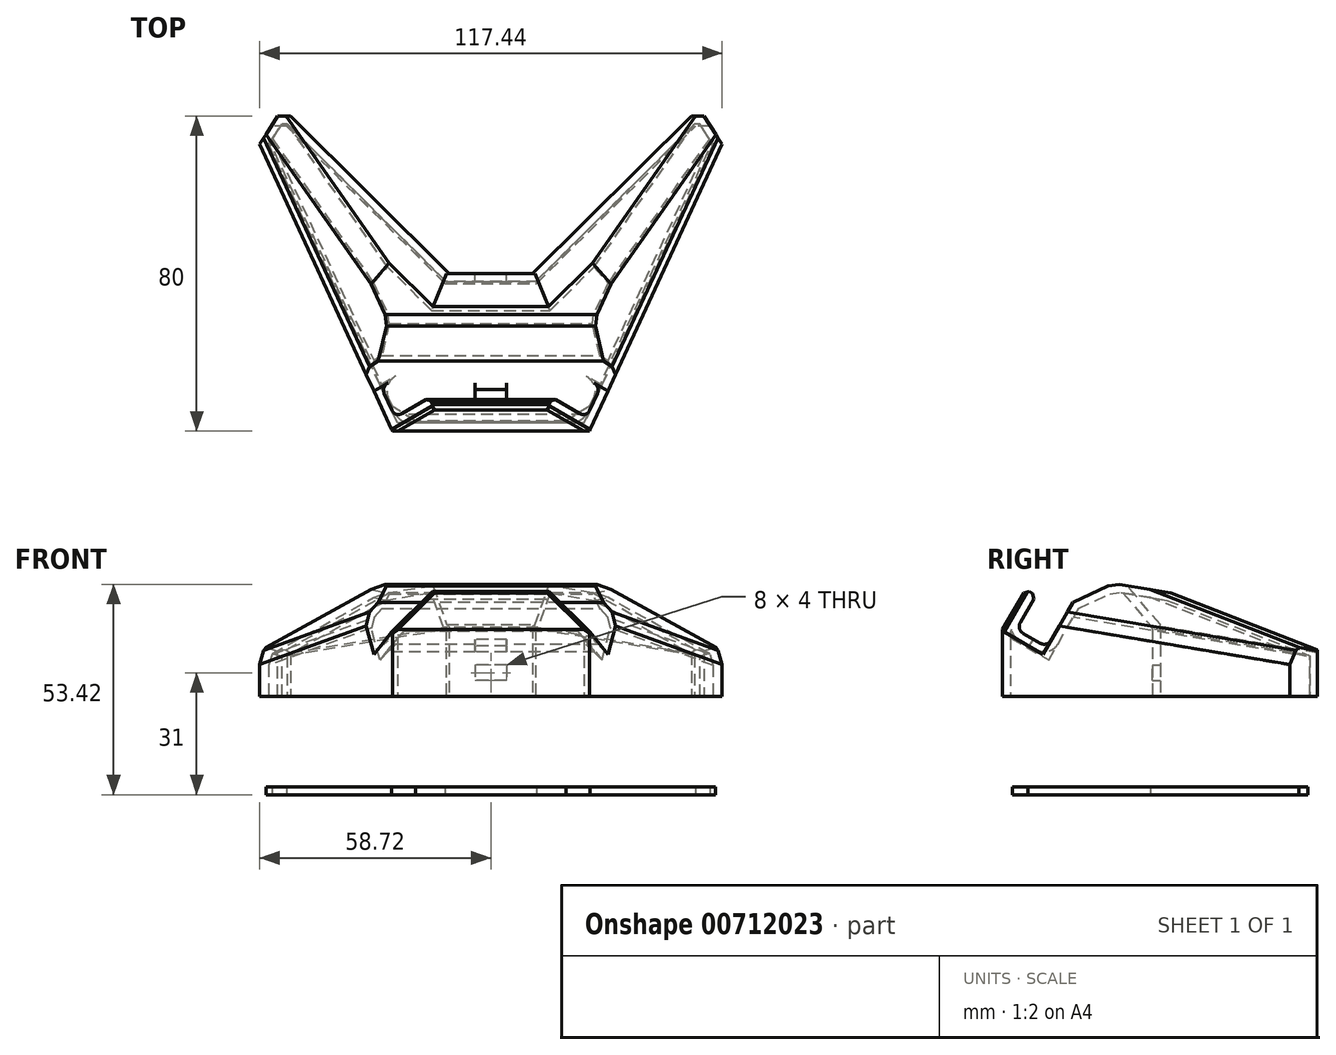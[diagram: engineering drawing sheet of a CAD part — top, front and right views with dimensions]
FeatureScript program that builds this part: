
annotation { "Feature Type Name" : "Feature", "Feature Type Description" : "" }
export const myFeature = defineFeature(function(context is Context, id is Id, definition is map)
    precondition{}
    {
        {
            var Q0;
            Q0=qCreatedBy(makeId("Right.planeOp"),FACE);
            var sketch = newSketch(context, id + "F0", { "sketchPlane" : qUnion([Q0])});
            skLineSegment(sketch, "E0", {"start": v(-41.49, 14.24) * mm, "end": v(-32.49, 29.83) * mm});
            skLineSegment(sketch, "E1", {"start": v(26.26, 20) * mm, "end": v(26.26, 0) * mm});
            skLineSegment(sketch, "E2", {"start": v(26.26, 0) * mm, "end": v(-53.74, 0) * mm});
            skLineSegment(sketch, "E3", {"start": v(-53.74, 0) * mm, "end": v(-53.74, 17) * mm});
            skLineSegment(sketch, "E4", {"start": v(-53.74, 17) * mm, "end": v(-47.88, 27.17) * mm});
            skLineSegment(sketch, "E5", {"start": v(-47.88, 27.17) * mm, "end": v(-45.28, 25.67) * mm});
            skLineSegment(sketch, "E6", {"start": v(-45.28, 25.67) * mm, "end": v(-49.28, 18.74) * mm});
            skLineSegment(sketch, "E7", {"start": v(-48.55, 16) * mm, "end": v(-44.22, 13.5) * mm});
            skPoint(sketch, "E8.visualSharp", {"position": v(-50.28, 17) * mm});
            skArc(sketch, "E8.filletArc", {"start": v(-49.28, 18.74) * mm, "mid": v(-49.48, 17.22) * mm, "end": v(-48.55, 16) * mm});
            skPoint(sketch, "E9.visualSharp", {"position": v(-42.49, 12.5) * mm});
            skArc(sketch, "E9.filletArc", {"start": v(-44.22, 13.5) * mm, "mid": v(-42.7, 13.3) * mm, "end": v(-41.49, 14.24) * mm});
            skLineSegment(sketch, "E10", {"start": v(-32.49, 29.83) * mm, "end": v(26.26, 20) * mm});
            skSolve(sketch);
        }
        {
            var Q0;
            Q0=makeQuery(id+"F0.imprint","IMPRINT",FACE,{"disambiguationData":[TD([[makeQuery(id+"F0.imprint","IMPRINT",EDGE,{"derivedFrom":sQuery(id+"F0.wireOp",EDGE,"E0")}),-1.0]])]});
            extrude(context, id + "F1", {"entities" : qUnion([Q0]), "endBound" : BoundingType.SYMMETRIC, "depth" : (114 + 10) * mm, "offsetDistance" : 25 * mm});
        }
        {
            var Q0;
            Q0=makeQuery(id+"F1.opExtrude","SWEPT_FACE",FACE,{"disambiguationData":[OSD([sQuery(id+"F0.wireOp",EDGE,"E2")])]});
            var sketch = newSketch(context, id + "F2", { "sketchPlane" : qUnion([Q0])});
            skLineSegment(sketch, "E11", {"start": v(62, 13.74) * mm, "end": v(-36.83, 13.74) * mm, "construction": true});
            skLineSegment(sketch, "E12", {"start": v(-62, -26.26) * mm, "end": v(-25, 53.74) * mm});
            skLineSegment(sketch, "E13", {"start": v(-10.58, 13.74) * mm, "end": v(-50.92, -26.26) * mm});
            skLineSegment(sketch, "E14.MirrorCS", {"start": v(10.58, 13.74) * mm, "end": v(50.92, -26.26) * mm});
            skLineSegment(sketch, "E15.MirrorCS", {"start": v(62, -26.26) * mm, "end": v(25, 53.74) * mm});
            skLineSegment(sketch, "E16", {"start": v(-10.58, 13.74) * mm, "end": v(10.58, 13.74) * mm});
            skSolve(sketch);
        }
        {
            var Q0;
            {var subQ0=sQuery(id+"F2.wireOp",EDGE,"E12");Q0=makeQuery(id+"F2.imprint","IMPRINT",FACE,{"disambiguationData":[TD([[makeQuery(id+"F2.imprint","IMPRINT",EDGE,{"derivedFrom":subQ0}),1.0]])]});}
            var Q1;
            {var subQ0=sQuery(id+"F2.wireOp",EDGE,"E13");Q1=makeQuery(id+"F2.imprint","IMPRINT",FACE,{"disambiguationData":[TD([[makeQuery(id+"F2.imprint","IMPRINT",EDGE,{"derivedFrom":subQ0}),1.0]])]});}
            var Q2;
            {var subQ0=sQuery(id+"F2.wireOp",EDGE,"E15.MirrorCS");Q2=makeQuery(id+"F2.imprint","IMPRINT",FACE,{"disambiguationData":[TD([[makeQuery(id+"F2.imprint","IMPRINT",EDGE,{"derivedFrom":subQ0}),-1.0]])]});}
            extrude(context, id + "F3", {"entities" : qUnion([Q0, Q1, Q2]), "operationType" : NewBodyOperationType.REMOVE, "endBound" : BoundingType.THROUGH_ALL, "oppositeDirection" : true, "depth" : 25 * mm, "offsetDistance" : 25 * mm});
        }
        {
            var Q0;
            Q0=makeQuery(id+"F3.boolean.opBoolean","INTERSECT",EDGE,{"derivedFrom":[makeQuery(id+"F1.opExtrude","SWEPT_FACE",FACE,{"disambiguationData":[OSD([sQuery(id+"F0.wireOp",EDGE,"E10")])]}),makeQuery(id+"F3.opExtrude","SWEPT_FACE",FACE,{"disambiguationData":[OSD([sQuery(id+"F2.wireOp",EDGE,"E12")])]})]});
            var Q1;
            Q1=makeQuery(id+"F3.boolean.opBoolean","INTERSECT",EDGE,{"derivedFrom":[makeQuery(id+"F1.opExtrude","SWEPT_FACE",FACE,{"disambiguationData":[OSD([sQuery(id+"F0.wireOp",EDGE,"E10")])]}),makeQuery(id+"F3.opExtrude","SWEPT_FACE",FACE,{"disambiguationData":[OSD([sQuery(id+"F2.wireOp",EDGE,"E13")])]})]});
            var Q2;
            Q2=makeQuery(id+"F3.boolean.opBoolean","INTERSECT",EDGE,{"derivedFrom":[makeQuery(id+"F1.opExtrude","SWEPT_FACE",FACE,{"disambiguationData":[OSD([sQuery(id+"F0.wireOp",EDGE,"E10")])]}),makeQuery(id+"F3.opExtrude","SWEPT_FACE",FACE,{"disambiguationData":[OSD([sQuery(id+"F2.wireOp",EDGE,"E16")])]})]});
            var Q3;
            Q3=makeQuery(id+"F3.boolean.opBoolean","INTERSECT",EDGE,{"derivedFrom":[makeQuery(id+"F1.opExtrude","SWEPT_FACE",FACE,{"disambiguationData":[OSD([sQuery(id+"F0.wireOp",EDGE,"E10")])]}),makeQuery(id+"F3.opExtrude","SWEPT_FACE",FACE,{"disambiguationData":[OSD([sQuery(id+"F2.wireOp",EDGE,"E14.MirrorCS")])]})]});
            var Q4;
            Q4=makeQuery(id+"F3.boolean.opBoolean","INTERSECT",EDGE,{"derivedFrom":[makeQuery(id+"F1.opExtrude","SWEPT_FACE",FACE,{"disambiguationData":[OSD([sQuery(id+"F0.wireOp",EDGE,"E10")])]}),makeQuery(id+"F3.opExtrude","SWEPT_FACE",FACE,{"disambiguationData":[OSD([sQuery(id+"F2.wireOp",EDGE,"E15.MirrorCS")])]})]});
            var Q5;
            Q5=makeQuery(id+"F1.opExtrude","SWEPT_EDGE",EDGE,{"disambiguationData":[OSD([sQuery(id+"F0.wireOp",EDGE,"E0"),sQuery(id+"F0.wireOp",EDGE,"E10")])]});
            chamfer(context, id + "F4", {"entities" : qUnion([Q0, Q1, Q2, Q3, Q4, Q5]), "width" : 10 * mm, "tangentPropagation" : true});
        }
        {
            var Q0;
            {var subQ0=makeQuery(id+"F1.opExtrude","SWEPT_FACE",FACE,{"disambiguationData":[OSD([sQuery(id+"F0.wireOp",EDGE,"E10")])]});Q0=makeQuery(id+"F4.opChamfer","BLEND_EDGE",EDGE,{"blendedFrom":[makeQuery(id+"F3.boolean.opBoolean","INTERSECT",EDGE,{"derivedFrom":[subQ0,makeQuery(id+"F3.opExtrude","SWEPT_FACE",FACE,{"disambiguationData":[OSD([sQuery(id+"F2.wireOp",EDGE,"E15.MirrorCS")])]})]}),makeQuery(id+"F3.boolean.opBoolean","INTERSECT",EDGE,{"derivedFrom":[subQ0,makeQuery(id+"F3.opExtrude","SWEPT_FACE",FACE,{"disambiguationData":[OSD([sQuery(id+"F2.wireOp",EDGE,"E14.MirrorCS")])]})]})],"blendedInto":[]});}
            var Q1;
            {var subQ0=makeQuery(id+"F1.opExtrude","SWEPT_FACE",FACE,{"disambiguationData":[OSD([sQuery(id+"F0.wireOp",EDGE,"E10")])]});Q1=makeQuery(id+"F4.opChamfer","BLEND_EDGE",EDGE,{"blendedFrom":[makeQuery(id+"F3.boolean.opBoolean","INTERSECT",EDGE,{"derivedFrom":[subQ0,makeQuery(id+"F3.opExtrude","SWEPT_FACE",FACE,{"disambiguationData":[OSD([sQuery(id+"F2.wireOp",EDGE,"E12")])]})]}),makeQuery(id+"F3.boolean.opBoolean","INTERSECT",EDGE,{"derivedFrom":[subQ0,makeQuery(id+"F3.opExtrude","SWEPT_FACE",FACE,{"disambiguationData":[OSD([sQuery(id+"F2.wireOp",EDGE,"E13")])]})]})],"blendedInto":[]});}
            var Q2;
            {var subQ0=makeQuery(id+"F3.opExtrude","SWEPT_FACE",FACE,{"disambiguationData":[OSD([sQuery(id+"F2.wireOp",EDGE,"E15.MirrorCS")])]});Q2=makeQuery(id+"F4.opChamfer","BLEND_EDGE",EDGE,{"blendedFrom":[makeQuery(id+"F3.boolean.opBoolean","INTERSECT",EDGE,{"derivedFrom":[makeQuery(id+"F1.opExtrude","SWEPT_FACE",FACE,{"disambiguationData":[OSD([sQuery(id+"F0.wireOp",EDGE,"E10")])]}),subQ0]}),makeQuery(id+"F3.boolean.opBoolean","COPY",FACE,{"derivedFrom":subQ0})],"blendedInto":[makeQuery(id+"F3.boolean.opBoolean","COPY",FACE,{"derivedFrom":subQ0})]});}
            var Q3;
            {var subQ0=makeQuery(id+"F3.opExtrude","SWEPT_FACE",FACE,{"disambiguationData":[OSD([sQuery(id+"F2.wireOp",EDGE,"E12")])]});Q3=makeQuery(id+"F4.opChamfer","BLEND_EDGE",EDGE,{"blendedFrom":[makeQuery(id+"F3.boolean.opBoolean","INTERSECT",EDGE,{"derivedFrom":[makeQuery(id+"F1.opExtrude","SWEPT_FACE",FACE,{"disambiguationData":[OSD([sQuery(id+"F0.wireOp",EDGE,"E10")])]}),subQ0]}),makeQuery(id+"F3.boolean.opBoolean","COPY",FACE,{"derivedFrom":subQ0})],"blendedInto":[makeQuery(id+"F3.boolean.opBoolean","COPY",FACE,{"derivedFrom":subQ0})]});}
            var Q4;
            {var subQ0=sQuery(id+"F0.wireOp",EDGE,"E10");Q4=makeQuery(id+"F4.opChamfer","BLEND_EDGE",EDGE,{"blendedFrom":[makeQuery(id+"F1.opExtrude","SWEPT_EDGE",EDGE,{"disambiguationData":[OSD([sQuery(id+"F0.wireOp",EDGE,"E0"),subQ0])]}),makeQuery(id+"F1.opExtrude","SWEPT_FACE",FACE,{"disambiguationData":[OSD([subQ0])]})],"blendedInto":[makeQuery(id+"F1.opExtrude","SWEPT_FACE",FACE,{"disambiguationData":[OSD([subQ0])]})]});}
            chamfer(context, id + "F5", {"entities" : qUnion([Q0, Q1, Q2, Q3, Q4]), "width" : 5 * mm, "tangentPropagation" : true});
        }
        {
            var Q0;
            Q0=makeQuery(id+"F3.boolean.opBoolean","INTERSECT",EDGE,{"derivedFrom":[makeQuery(id+"F1.opExtrude","SWEPT_FACE",FACE,{"disambiguationData":[OSD([sQuery(id+"F0.wireOp",EDGE,"E5")])]}),makeQuery(id+"F3.opExtrude","SWEPT_FACE",FACE,{"disambiguationData":[OSD([sQuery(id+"F2.wireOp",EDGE,"E15.MirrorCS")])]})]});
            var Q1;
            Q1=makeQuery(id+"F3.boolean.opBoolean","INTERSECT",EDGE,{"derivedFrom":[makeQuery(id+"F1.opExtrude","SWEPT_FACE",FACE,{"disambiguationData":[OSD([sQuery(id+"F0.wireOp",EDGE,"E5")])]}),makeQuery(id+"F3.opExtrude","SWEPT_FACE",FACE,{"disambiguationData":[OSD([sQuery(id+"F2.wireOp",EDGE,"E12")])]})]});
            var Q2;
            Q2=makeQuery(id+"F3.boolean.opBoolean","COPY",EDGE,{"derivedFrom":makeQuery(id+"F3.opExtrude","SWEPT_EDGE",EDGE,{"disambiguationData":[OSD([sQuery(id+"F0.wireOp",EDGE,"E2"),sQuery(id+"F0.wireOp",EDGE,"E3"),sQuery(id+"F2.wireOp",EDGE,"E15.MirrorCS")])]})});
            var Q3;
            Q3=makeQuery(id+"F3.boolean.opBoolean","COPY",EDGE,{"derivedFrom":makeQuery(id+"F3.opExtrude","SWEPT_EDGE",EDGE,{"disambiguationData":[OSD([sQuery(id+"F0.wireOp",EDGE,"E2"),sQuery(id+"F0.wireOp",EDGE,"E3"),sQuery(id+"F2.wireOp",EDGE,"E12")])]})});
            chamfer(context, id + "F6", {"entities" : qUnion([Q0, Q1, Q2, Q3]), "width" : 10 * mm, "tangentPropagation" : true});
        }
        {
            var Q0;
            {var subQ0=sQuery(id+"F0.wireOp",EDGE,"E1");Q0=makeQuery(id+"F3.boolean.opBoolean","MERGE",EDGE,{"derivedFrom":[makeQuery(id+"F1.opExtrude","CAP_EDGE",EDGE,{"disambiguationData":[OSD([subQ0])],"isStart":false}),makeQuery(id+"F3.opExtrude","SWEPT_EDGE",EDGE,{"disambiguationData":[OSD([subQ0,sQuery(id+"F0.wireOp",EDGE,"E2"),sQuery(id+"F2.wireOp",EDGE,"E15.MirrorCS")])]})]});}
            var Q1;
            {var subQ0=sQuery(id+"F0.wireOp",EDGE,"E1");Q1=makeQuery(id+"F3.boolean.opBoolean","MERGE",EDGE,{"derivedFrom":[makeQuery(id+"F1.opExtrude","CAP_EDGE",EDGE,{"disambiguationData":[OSD([subQ0])],"isStart":true}),makeQuery(id+"F3.opExtrude","SWEPT_EDGE",EDGE,{"disambiguationData":[OSD([subQ0,sQuery(id+"F0.wireOp",EDGE,"E2"),sQuery(id+"F2.wireOp",EDGE,"E12")])]})]});}
            chamfer(context, id + "F7", {"entities" : qUnion([Q0, Q1]), "width" : 5 * mm, "tangentPropagation" : true});
        }
        {
            var Q0;
            Q0=makeQuery(id+"F1.opExtrude","SWEPT_FACE",FACE,{"disambiguationData":[OSD([sQuery(id+"F0.wireOp",EDGE,"E2")])]});
            shell(context, id + "F8", {"entities" : qUnion([Q0]), "thickness" : 2 * mm});
        }
        {
            var Q0;
            Q0=makeQuery(id+"F3.boolean.opBoolean","COPY",FACE,{"derivedFrom":makeQuery(id+"F3.opExtrude","SWEPT_FACE",FACE,{"disambiguationData":[OSD([sQuery(id+"F2.wireOp",EDGE,"E16")])]})});
            var sketch = newSketch(context, id + "F9", { "sketchPlane" : qUnion([Q0])});
            skLineSegment(sketch, "E17.bottom", {"start": v(-4, 8) * mm, "end": v(4, 8) * mm});
            skLineSegment(sketch, "E17.top", {"start": v(-4, 4) * mm, "end": v(4, 4) * mm});
            skLineSegment(sketch, "E17.left", {"start": v(-4, 8) * mm, "end": v(-4, 4) * mm});
            skLineSegment(sketch, "E17.right", {"start": v(4, 8) * mm, "end": v(4, 4) * mm});
            skLineSegment(sketch, "E18", {"start": v(0, 4) * mm, "end": v(0, 0) * mm, "construction": true});
            skSolve(sketch);
        }
        {
            var Q0;
            Q0 = qSketchRegion(id + "F9", true);
            var Q1;
            Q1=makeQuery(id+"F8.opShell","OFFSET_FACE",FACE,{"disambiguationData":[OSD([sQuery(id+"F2.wireOp",EDGE,"E16")])]});
            extrude(context, id + "F10", {"entities" : qUnion([Q0]), "operationType" : NewBodyOperationType.REMOVE, "endBound" : BoundingType.UP_TO_SURFACE, "oppositeDirection" : true, "depth" : 25 * mm, "endBoundEntityFace" : qUnion([Q1]), "offsetDistance" : 25 * mm});
        }
        {
            var Q0;
            Q0=makeQuery(id+"F1.opExtrude","SWEPT_FACE",FACE,{"disambiguationData":[OSD([sQuery(id+"F0.wireOp",EDGE,"E7")])]});
            var sketch = newSketch(context, id + "F11", { "sketchPlane" : qUnion([Q0])});
            skLineSegment(sketch, "E19.bottom", {"start": v(4, -47.05) * mm, "end": v(-4, -47.05) * mm});
            skLineSegment(sketch, "E19.top", {"start": v(4, -43.05) * mm, "end": v(-4, -43.05) * mm});
            skLineSegment(sketch, "E19.left", {"start": v(4, -47.05) * mm, "end": v(4, -43.05) * mm});
            skLineSegment(sketch, "E19.right", {"start": v(-4, -47.05) * mm, "end": v(-4, -43.05) * mm});
            skPoint(sketch, "E20.endSnap0", {"position": v(0, -50.05) * mm});
            skLineSegment(sketch, "E21.0", {"start": v(30.67, -43.05) * mm, "end": v(-30.67, -43.05) * mm});
            skLineSegment(sketch, "E22", {"start": v(0, -43.05) * mm, "end": v(0, -43.05) * mm});
            skSolve(sketch);
        }
        {
            var Q0;
            Q0 = qSketchRegion(id + "F11", true);
            extrude(context, id + "F12", {"entities" : qUnion([Q0]), "operationType" : NewBodyOperationType.REMOVE, "endBound" : BoundingType.SYMMETRIC, "oppositeDirection" : true, "depth" : 5 * mm, "offsetDistance" : 25 * mm});
        }
        {
            var Q0;
            Q0=qCreatedBy(makeId("Top.planeOp"),FACE);
            cPlane(context, id + "F13", {"entities" : qUnion([Q0]), "cplaneType" : CPlaneType.OFFSET, "offset" : 25 * mm, "oppositeDirection" : true, "width" : 150 * mm, "height" : 150 * mm});
        }
        {
            var Q0;
            Q0=qCreatedBy(id+"F13.planeOp",FACE);
            var sketch = newSketch(context, id + "F14", { "sketchPlane" : qUnion([Q0])});
            skLineSegment(sketch, "E23.0", {"start": v(-11.61, -16.24) * mm, "end": v(11.61, -16.24) * mm});
            skLineSegment(sketch, "E23.1", {"start": v(25.2, -47.34) * mm, "end": v(19.1, -51.24) * mm});
            skLineSegment(sketch, "E23.2", {"start": v(57.06, 21.52) * mm, "end": v(25.2, -47.34) * mm});
            skLineSegment(sketch, "E23.3", {"start": v(55.63, 23.76) * mm, "end": v(57.06, 21.52) * mm});
            skLineSegment(sketch, "E23.4", {"start": v(55.63, 23.76) * mm, "end": v(51.95, 23.76) * mm});
            skLineSegment(sketch, "E23.5", {"start": v(19.1, -51.24) * mm, "end": v(-19.1, -51.24) * mm});
            skLineSegment(sketch, "E23.6", {"start": v(11.61, -16.24) * mm, "end": v(51.95, 23.76) * mm});
            skLineSegment(sketch, "E23.7", {"start": v(-19.1, -51.24) * mm, "end": v(-25.2, -47.34) * mm});
            skLineSegment(sketch, "E23.8", {"start": v(-57.06, 21.52) * mm, "end": v(-25.2, -47.34) * mm});
            skLineSegment(sketch, "E23.9", {"start": v(-57.06, 21.52) * mm, "end": v(-55.63, 23.76) * mm});
            skLineSegment(sketch, "E23.10", {"start": v(-51.95, 23.76) * mm, "end": v(-55.63, 23.76) * mm});
            skLineSegment(sketch, "E23.11", {"start": v(-11.61, -16.24) * mm, "end": v(-51.95, 23.76) * mm});
            skSolve(sketch);
        }
        {
            var Q0;
            Q0=makeQuery(id+"F14.imprint","IMPRINT",FACE,{"disambiguationData":[TD([[makeQuery(id+"F14.imprint","IMPRINT",EDGE,{"derivedFrom":sQuery(id+"F14.wireOp",EDGE,"E23.0")}),-1.0]])]});
            extrude(context, id + "F15", {"entities" : qUnion([Q0]), "depth" : 2 * mm, "offsetDistance" : 25 * mm});
        }
        {
            var Q0;
            Q0=makeQuery(id+"F1.opExtrude","SWEPT_EDGE",EDGE,{"disambiguationData":[OSD([sQuery(id+"F0.wireOp",EDGE,"E4"),sQuery(id+"F0.wireOp",EDGE,"E5")])]});
            var Q1;
            Q1=makeQuery(id+"F1.opExtrude","SWEPT_EDGE",EDGE,{"disambiguationData":[OSD([sQuery(id+"F0.wireOp",EDGE,"E5"),sQuery(id+"F0.wireOp",EDGE,"E6")])]});
            var Q2;
            Q2=makeQuery(id+"F6.opChamfer","BLEND_EDGE",EDGE,{"blendedFrom":[makeQuery(id+"F3.boolean.opBoolean","INTERSECT",EDGE,{"derivedFrom":[makeQuery(id+"F1.opExtrude","SWEPT_FACE",FACE,{"disambiguationData":[OSD([sQuery(id+"F0.wireOp",EDGE,"E5")])]}),makeQuery(id+"F3.opExtrude","SWEPT_FACE",FACE,{"disambiguationData":[OSD([sQuery(id+"F2.wireOp",EDGE,"E12")])]})]}),makeQuery(id+"F1.opExtrude","SWEPT_FACE",FACE,{"disambiguationData":[OSD([sQuery(id+"F0.wireOp",EDGE,"E4")])]})],"blendedInto":[makeQuery(id+"F1.opExtrude","SWEPT_FACE",FACE,{"disambiguationData":[OSD([sQuery(id+"F0.wireOp",EDGE,"E4")])]})]});
            var Q3;
            Q3=makeQuery(id+"F6.opChamfer","BLEND_EDGE",EDGE,{"blendedFrom":[makeQuery(id+"F3.boolean.opBoolean","INTERSECT",EDGE,{"derivedFrom":[makeQuery(id+"F1.opExtrude","SWEPT_FACE",FACE,{"disambiguationData":[OSD([sQuery(id+"F0.wireOp",EDGE,"E5")])]}),makeQuery(id+"F3.opExtrude","SWEPT_FACE",FACE,{"disambiguationData":[OSD([sQuery(id+"F2.wireOp",EDGE,"E15.MirrorCS")])]})]}),makeQuery(id+"F1.opExtrude","SWEPT_FACE",FACE,{"disambiguationData":[OSD([sQuery(id+"F0.wireOp",EDGE,"E4")])]})],"blendedInto":[makeQuery(id+"F1.opExtrude","SWEPT_FACE",FACE,{"disambiguationData":[OSD([sQuery(id+"F0.wireOp",EDGE,"E4")])]})]});
            chamfer(context, id + "F16", {"entities" : qUnion([Q0, Q1, Q2, Q3]), "width" : 1 * mm, "tangentPropagation" : true});
        }
    });
